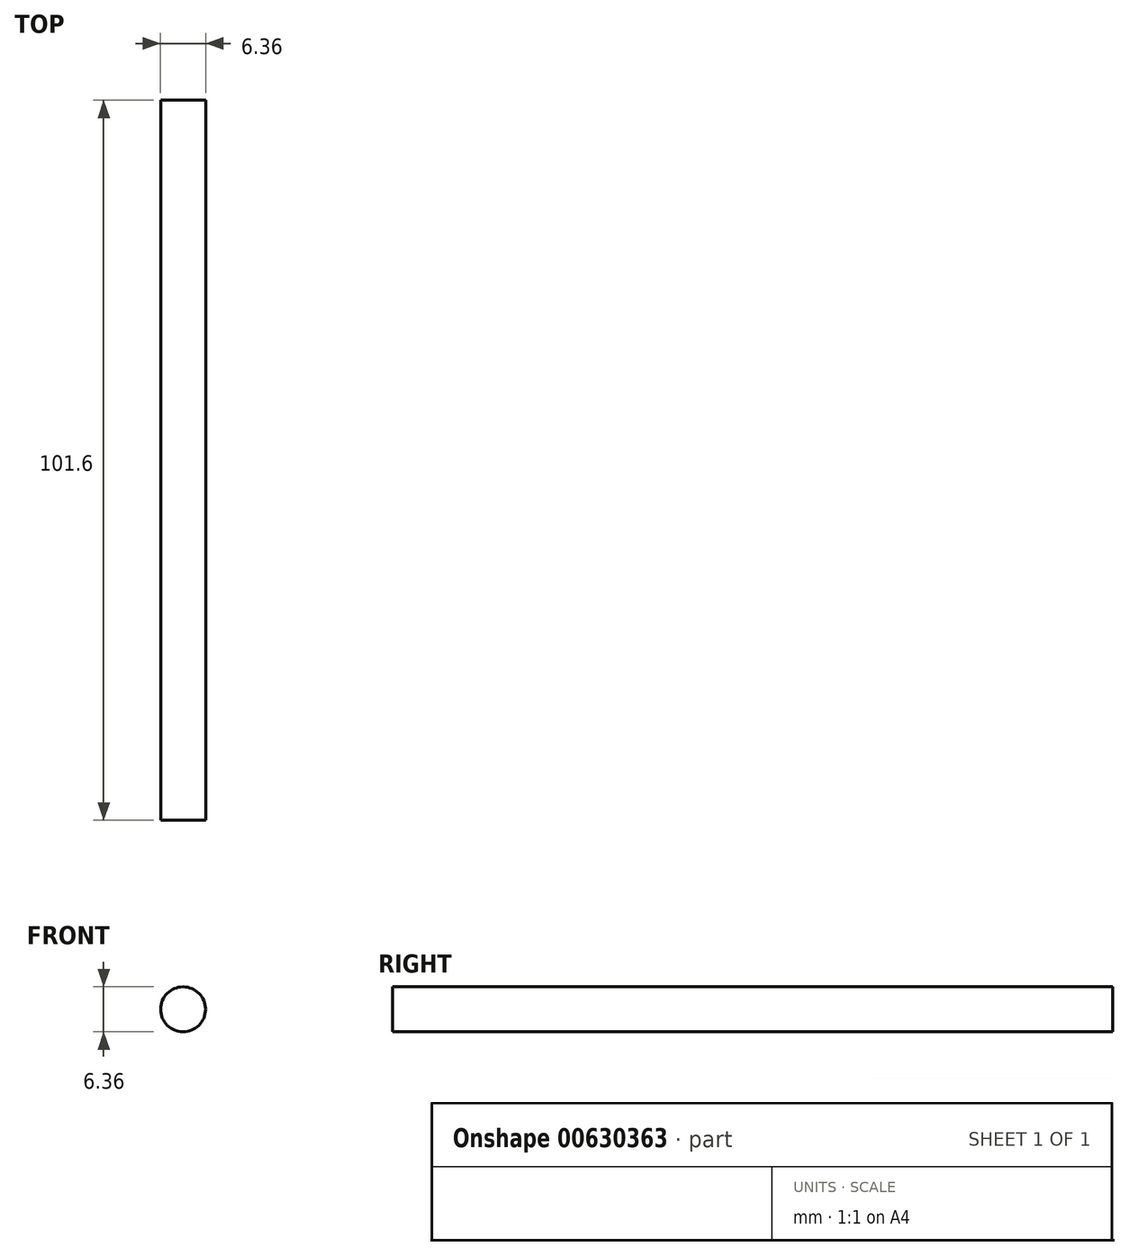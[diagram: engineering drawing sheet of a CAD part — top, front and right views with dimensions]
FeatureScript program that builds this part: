
annotation { "Feature Type Name" : "Feature", "Feature Type Description" : "" }
export const myFeature = defineFeature(function(context is Context, id is Id, definition is map)
    precondition{}
    {
        {
            var Q0;
            Q0=qCreatedBy(makeId("Front.planeOp"),FACE);
            var sketch = newSketch(context, id + "F0", { "sketchPlane" : qUnion([Q0])});
            skCircle(sketch, "E0", {"center": v(0, 0) * mm, "radius": 3.18 * mm});
            skSolve(sketch);
        }
        {
            var Q0;
            Q0 = qSketchRegion(id + "F0", true);
            extrude(context, id + "F1", {"entities" : qUnion([Q0]), "oppositeDirection" : true, "depth" : 101.6 * mm, "offsetDistance" : 25.4 * mm});
        }
    });
